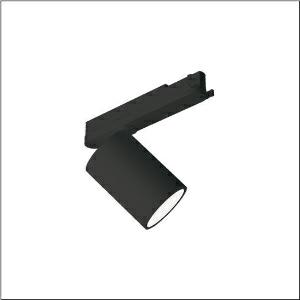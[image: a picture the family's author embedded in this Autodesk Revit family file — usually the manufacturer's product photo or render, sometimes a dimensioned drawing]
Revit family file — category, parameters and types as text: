
# Revit family: spot_31_51sf32mad4b
name_source: partatom
category: Lighting Fixtures
units: mm (PartAtom-declared; Revit-internal decimal feet)

## family parameters
Cut with Voids When Loaded = No
Host = Face
Light Source = No
Part Type = Normal
Room Calculation Point = No
Round Connector Dimension = Use Diameter
Shared = No

## types (1)
- --- (1 x LED, 5140 lm, 41.6 W, 4000K)
    Apparent Load = 42 VA
    CIE Flux Codes = 93 97 99 100 100
    Color Rendering = 90
    Color Temperature = 4000K
    Default Elevation = 1800 mm
    Description = Spot 31, directional spotlight, light control with lens, of PMMA, LED rated luminous flux: 4.930lm, light colour: 940, control gear: ECG Multilumen, with 3-phase adapter, mains connection: 220..240V, AC, 50/60Hz, of aluminium, jet black (RAL 9005), length: 213mm, diameter: 90mm, protection rating (complete): IP20, insulation class (complete): insulation class I (protective earthing), certification: CE, impact resistance: IK02, permissible ambient temperature for indoor applications: -20..+40°C, packaging unit: 1 piece
    Height = 175 mm
    Lamp = 1 x LED
    Lamp Light Flux = 5140 lm
    Lamp Power = 41.6 W
    Lamp count = 1
    Length = 90 mm
    Luminous efficacy = 124 lm/W
    Manufacturer = Siteco
    ModVariant = No
    Model = 51SF32MAD4B
    Mounting Place = Ceiling
    Mounting Type = Pendant
    Number of Poles = 1
    OnlyDefault = Yes
    Power Factor = 1
    Product Name = Spot 31
    Product group = directional spotlight
    ProductGroupID = 905
    Protection Class = Protection class I
    Protection Degree = IP 20
    RLX_Detail_Level = 1
    RLX_Emergency_Light_Flux = 0 lm
    RLX_Emergency_Type = 0
    RLX_Emergency_Type_DB = No
    RlxData = <blob elided: 20913 chars, md5=2fcfd6e2>
    Socket = socket
    Standby Power = 0 W
    System Light Flux = 5140 lm
    System Power = 42 W
    Type Comments = factory setting: luminous flux: 100 % | (ON | ON | ON | ON) | 1050 mA
    Type Image = l_1273723.jpg
    URL = http://relux.com
    VarID = @adj_078537
    Voltage = 0 V
    Weight = 0.00 kg
    Width = 0 mm  [stored 0 ft]

note: [stored X ft] marks values corroborated as IEEE doubles in the binary element streams (Revit-internal decimal feet)

## geometry (parser evidence)
native form markers: Blend x4, Sweep x12
no freeform markers — native parametric forms only
